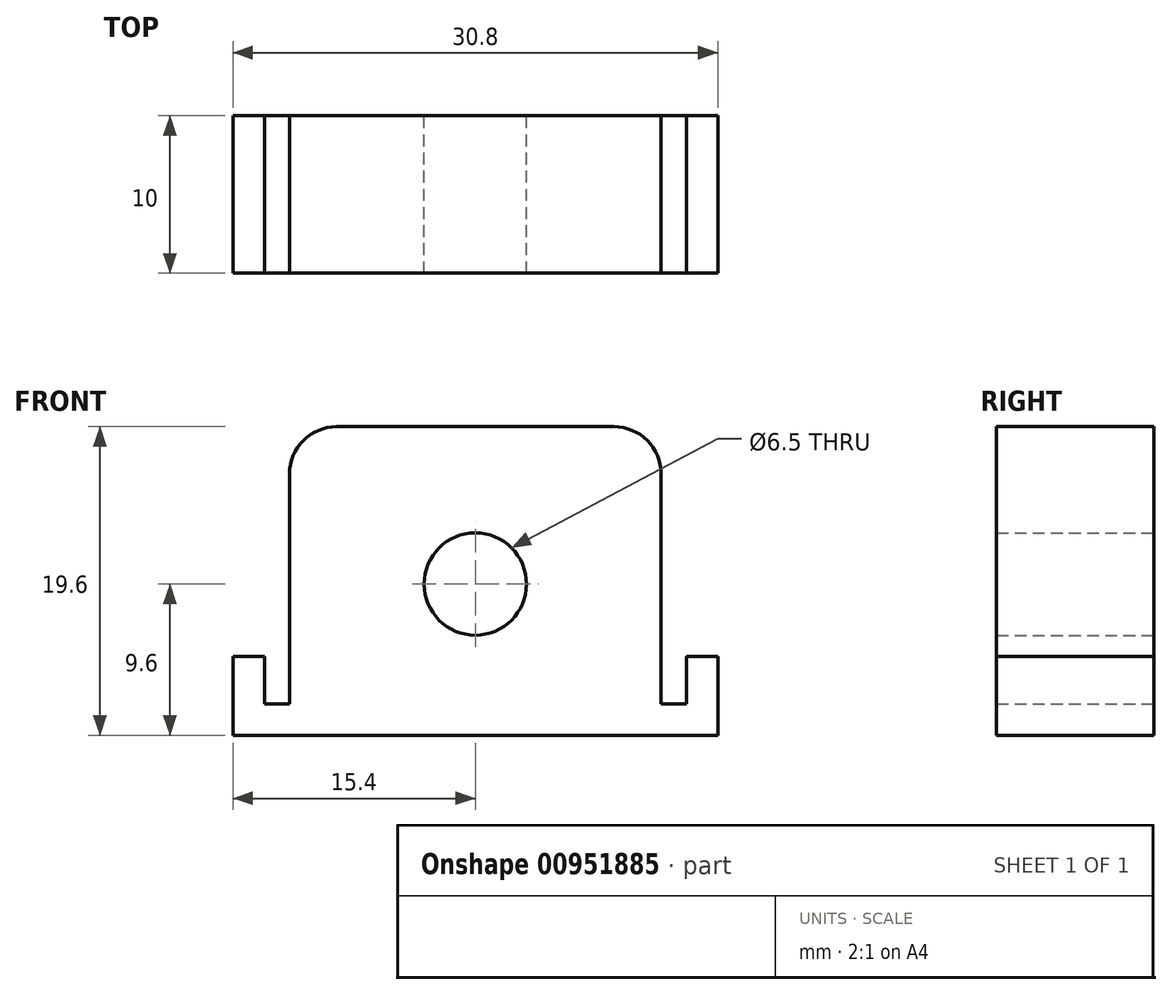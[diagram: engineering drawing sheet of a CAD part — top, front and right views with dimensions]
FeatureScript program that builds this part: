
annotation { "Feature Type Name" : "Feature", "Feature Type Description" : "" }
export const myFeature = defineFeature(function(context is Context, id is Id, definition is map)
    precondition{}
    {
        {
            var Q0;
            Q0=qCreatedBy(makeId("Front.planeOp"),FACE);
            var sketch = newSketch(context, id + "F0", { "sketchPlane" : qUnion([Q0])});
            skLineSegment(sketch, "E0.0", {"start": v(-13.4, -6.54) * mm, "end": v(-13.4, -9.5) * mm});
            skLineSegment(sketch, "E0.2", {"start": v(13.4, -6.54) * mm, "end": v(13.4, -9.5) * mm});
            skLineSegment(sketch, "E1.0", {"start": v(-11.8, 5.05) * mm, "end": v(-11.8, -9.5) * mm});
            skLineSegment(sketch, "E1.1", {"start": v(-8.8, 8.05) * mm, "end": v(8.8, 8.05) * mm});
            skLineSegment(sketch, "E1.2", {"start": v(11.8, 5.05) * mm, "end": v(11.8, -9.5) * mm});
            skArc(sketch, "E2.filletArc", {"start": v(-8.8, 8.05) * mm, "mid": v(-10.92, 7.17) * mm, "end": v(-11.8, 5.05) * mm});
            skArc(sketch, "E3.filletArc", {"start": v(11.8, 5.05) * mm, "mid": v(10.92, 7.17) * mm, "end": v(8.8, 8.05) * mm});
            skLineSegment(sketch, "E4", {"start": v(-13.4, -9.5) * mm, "end": v(-13.4, -9.55) * mm});
            skLineSegment(sketch, "E5", {"start": v(-13.4, -9.55) * mm, "end": v(-11.8, -9.55) * mm});
            skLineSegment(sketch, "E6", {"start": v(-11.8, -9.55) * mm, "end": v(-11.8, -9.5) * mm});
            skLineSegment(sketch, "E7", {"start": v(11.8, -9.5) * mm, "end": v(11.8, -9.55) * mm});
            skLineSegment(sketch, "E8", {"start": v(11.8, -9.55) * mm, "end": v(13.4, -9.55) * mm});
            skLineSegment(sketch, "E9", {"start": v(13.4, -9.55) * mm, "end": v(13.4, -9.5) * mm});
            skLineSegment(sketch, "E10", {"start": v(-13.4, -6.54) * mm, "end": v(-15.4, -6.54) * mm});
            skLineSegment(sketch, "E11", {"start": v(-15.4, -6.54) * mm, "end": v(-15.4, -11.55) * mm});
            skLineSegment(sketch, "E12", {"start": v(13.4, -6.54) * mm, "end": v(15.4, -6.54) * mm});
            skLineSegment(sketch, "E13", {"start": v(15.4, -6.54) * mm, "end": v(15.4, -11.55) * mm});
            skLineSegment(sketch, "E14", {"start": v(-15.4, -11.55) * mm, "end": v(15.4, -11.55) * mm});
            skCircle(sketch, "E15", {"center": v(0, -1.95) * mm, "radius": 3.25 * mm});
            skSolve(sketch);
        }
        {
            var Q0;
            Q0=makeQuery(id+"F0.imprint","IMPRINT",FACE,{"disambiguationData":[TD([[makeQuery(id+"F0.imprint","IMPRINT",EDGE,{"derivedFrom":sQuery(id+"F0.wireOp",EDGE,"E0.0")}),-1.0]])]});
            extrude(context, id + "F1", {"entities" : qUnion([Q0]), "depth" : 10 * mm, "offsetDistance" : 25 * mm});
        }
    });
